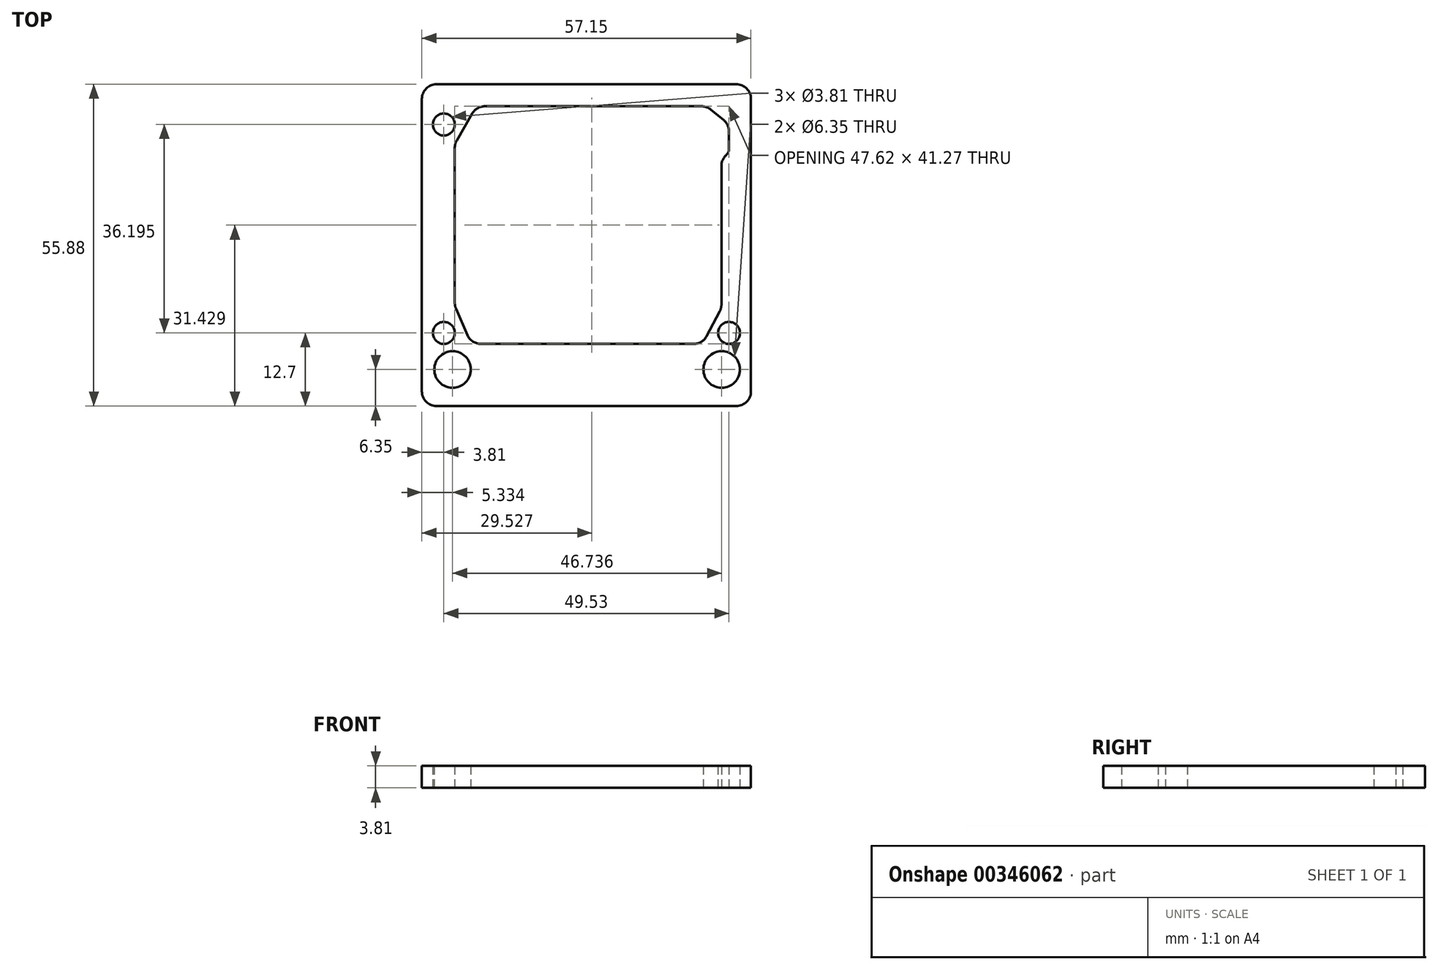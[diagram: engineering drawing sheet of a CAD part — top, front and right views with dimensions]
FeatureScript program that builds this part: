
annotation { "Feature Type Name" : "Feature", "Feature Type Description" : "" }
export const myFeature = defineFeature(function(context is Context, id is Id, definition is map)
    precondition{}
    {
        {
            var Q0;
            Q0=qCreatedBy(makeId("Top.planeOp"),FACE);
            var sketch = newSketch(context, id + "F0", { "sketchPlane" : qUnion([Q0])});
            skCircle(sketch, "E0", {"center": v(0, 0) * mm, "radius": 1.9 * mm});
            skCircle(sketch, "E1", {"center": v(0, 36.2) * mm, "radius": 1.9 * mm});
            skCircle(sketch, "E2", {"center": v(49.53, 0) * mm, "radius": 1.9 * mm});
            skLineSegment(sketch, "E3.bottom", {"start": v(0, 0) * mm, "end": v(1.52, 0) * mm, "construction": true});
            skLineSegment(sketch, "E3.top", {"start": v(0, -6.35) * mm, "end": v(1.52, -6.35) * mm, "construction": true});
            skCircle(sketch, "E4", {"center": v(1.52, -6.35) * mm, "radius": 3.18 * mm});
            skCircle(sketch, "E5", {"center": v(48.26, -6.35) * mm, "radius": 3.18 * mm});
            skLineSegment(sketch, "E6.bottom", {"start": v(0, 0) * mm, "end": v(-3.81, 0) * mm, "construction": true});
            skLineSegment(sketch, "E6.top", {"start": v(0, -12.7) * mm, "end": v(-3.8, -12.7) * mm, "construction": true});
            skLineSegment(sketch, "E6.left", {"start": v(0, 0) * mm, "end": v(0, -12.7) * mm, "construction": true});
            skLineSegment(sketch, "E6.right", {"start": v(-3.81, 0) * mm, "end": v(-3.8, -12.7) * mm, "construction": true});
            skLineSegment(sketch, "E7.bottom", {"start": v(-3.8, -12.7) * mm, "end": v(53.34, -12.7) * mm});
            skLineSegment(sketch, "E7.top", {"start": v(-3.81, 43.18) * mm, "end": v(53.34, 43.18) * mm});
            skLineSegment(sketch, "E7.left", {"start": v(-3.8, -12.7) * mm, "end": v(-3.8, 43.18) * mm});
            skLineSegment(sketch, "E7.right", {"start": v(53.34, -12.7) * mm, "end": v(53.34, 43.18) * mm});
            skLineSegment(sketch, "E8", {"start": v(1.9, 4.7) * mm, "end": v(4.77, -1.9) * mm});
            skLineSegment(sketch, "E9", {"start": v(4.77, -1.9) * mm, "end": v(44.94, -1.9) * mm});
            skLineSegment(sketch, "E10", {"start": v(44.94, -1.9) * mm, "end": v(48.21, 4.3) * mm});
            skLineSegment(sketch, "E11", {"start": v(48.21, 4.3) * mm, "end": v(48.21, 30.09) * mm});
            skLineSegment(sketch, "E12", {"start": v(48.21, 30.09) * mm, "end": v(49.53, 31.36) * mm});
            skLineSegment(sketch, "E13", {"start": v(49.53, 31.36) * mm, "end": v(49.53, 36.2) * mm});
            skLineSegment(sketch, "E14", {"start": v(49.53, 36.2) * mm, "end": v(45.66, 39.36) * mm});
            skLineSegment(sketch, "E15", {"start": v(45.66, 39.36) * mm, "end": v(5.65, 39.36) * mm});
            skLineSegment(sketch, "E16", {"start": v(5.65, 39.36) * mm, "end": v(1.9, 32.8) * mm});
            skLineSegment(sketch, "E17", {"start": v(1.9, 32.8) * mm, "end": v(1.9, 4.7) * mm});
            skSolve(sketch);
        }
        {
            var Q0;
            Q0=makeQuery(id+"F0.imprint","IMPRINT",FACE,{"disambiguationData":[TD([[makeQuery(id+"F0.imprint","IMPRINT",EDGE,{"derivedFrom":sQuery(id+"F0.wireOp",EDGE,"E0")}),-1.0]])]});
            extrude(context, id + "F1", {"entities" : qUnion([Q0]), "depth" : 3.8 * mm});
        }
        {
            var Q0;
            Q0=makeQuery(id+"F1.opExtrude","SWEPT_EDGE",EDGE,{"disambiguationData":[OSD([sQuery(id+"F0.wireOp",EDGE,"E7.bottom"),sQuery(id+"F0.wireOp",EDGE,"E7.left")])]});
            var Q1;
            Q1=makeQuery(id+"F1.opExtrude","SWEPT_EDGE",EDGE,{"disambiguationData":[OSD([sQuery(id+"F0.wireOp",EDGE,"E7.top"),sQuery(id+"F0.wireOp",EDGE,"E7.left")])]});
            var Q2;
            Q2=makeQuery(id+"F1.opExtrude","SWEPT_EDGE",EDGE,{"disambiguationData":[OSD([sQuery(id+"F0.wireOp",EDGE,"E7.bottom"),sQuery(id+"F0.wireOp",EDGE,"E7.right")])]});
            var Q3;
            Q3=makeQuery(id+"F1.opExtrude","SWEPT_EDGE",EDGE,{"disambiguationData":[OSD([sQuery(id+"F0.wireOp",EDGE,"E7.top"),sQuery(id+"F0.wireOp",EDGE,"E7.right")])]});
            var Q4;
            Q4=makeQuery(id+"F1.opExtrude","SWEPT_EDGE",EDGE,{"disambiguationData":[OSD([sQuery(id+"F0.wireOp",EDGE,"E16"),sQuery(id+"F0.wireOp",EDGE,"E17")])]});
            var Q5;
            Q5=makeQuery(id+"F1.opExtrude","SWEPT_EDGE",EDGE,{"disambiguationData":[OSD([sQuery(id+"F0.wireOp",EDGE,"E15"),sQuery(id+"F0.wireOp",EDGE,"E16")])]});
            var Q6;
            Q6=makeQuery(id+"F1.opExtrude","SWEPT_EDGE",EDGE,{"disambiguationData":[OSD([sQuery(id+"F0.wireOp",EDGE,"E8"),sQuery(id+"F0.wireOp",EDGE,"E17")])]});
            var Q7;
            Q7=makeQuery(id+"F1.opExtrude","SWEPT_EDGE",EDGE,{"disambiguationData":[OSD([sQuery(id+"F0.wireOp",EDGE,"E8"),sQuery(id+"F0.wireOp",EDGE,"E9")])]});
            var Q8;
            Q8=makeQuery(id+"F1.opExtrude","SWEPT_EDGE",EDGE,{"disambiguationData":[OSD([sQuery(id+"F0.wireOp",EDGE,"E14"),sQuery(id+"F0.wireOp",EDGE,"E15")])]});
            var Q9;
            Q9=makeQuery(id+"F1.opExtrude","SWEPT_EDGE",EDGE,{"disambiguationData":[OSD([sQuery(id+"F0.wireOp",EDGE,"E13"),sQuery(id+"F0.wireOp",EDGE,"E14")])]});
            var Q10;
            Q10=makeQuery(id+"F1.opExtrude","SWEPT_EDGE",EDGE,{"disambiguationData":[OSD([sQuery(id+"F0.wireOp",EDGE,"E11"),sQuery(id+"F0.wireOp",EDGE,"E12")])]});
            var Q11;
            Q11=makeQuery(id+"F1.opExtrude","SWEPT_EDGE",EDGE,{"disambiguationData":[OSD([sQuery(id+"F0.wireOp",EDGE,"E10"),sQuery(id+"F0.wireOp",EDGE,"E11")])]});
            var Q12;
            Q12=makeQuery(id+"F1.opExtrude","SWEPT_EDGE",EDGE,{"disambiguationData":[OSD([sQuery(id+"F0.wireOp",EDGE,"E9"),sQuery(id+"F0.wireOp",EDGE,"E10")])]});
            fillet(context, id + "F2", {"entities" : qUnion([Q0, Q1, Q2, Q3, Q4, Q5, Q6, Q7, Q8, Q9, Q10, Q11, Q12]), "radius" : 2.54 * mm, "tangentPropagation" : true, "allowEdgeOverflow" : false});
        }
        {
            var Q0;
            Q0=makeQuery(id+"F1.opExtrude","SWEPT_EDGE",EDGE,{"disambiguationData":[OSD([sQuery(id+"F0.wireOp",EDGE,"E12"),sQuery(id+"F0.wireOp",EDGE,"E13")])]});
            fillet(context, id + "F3", {"entities" : qUnion([Q0]), "radius" : 1.27 * mm, "tangentPropagation" : true, "allowEdgeOverflow" : false});
        }
    });
